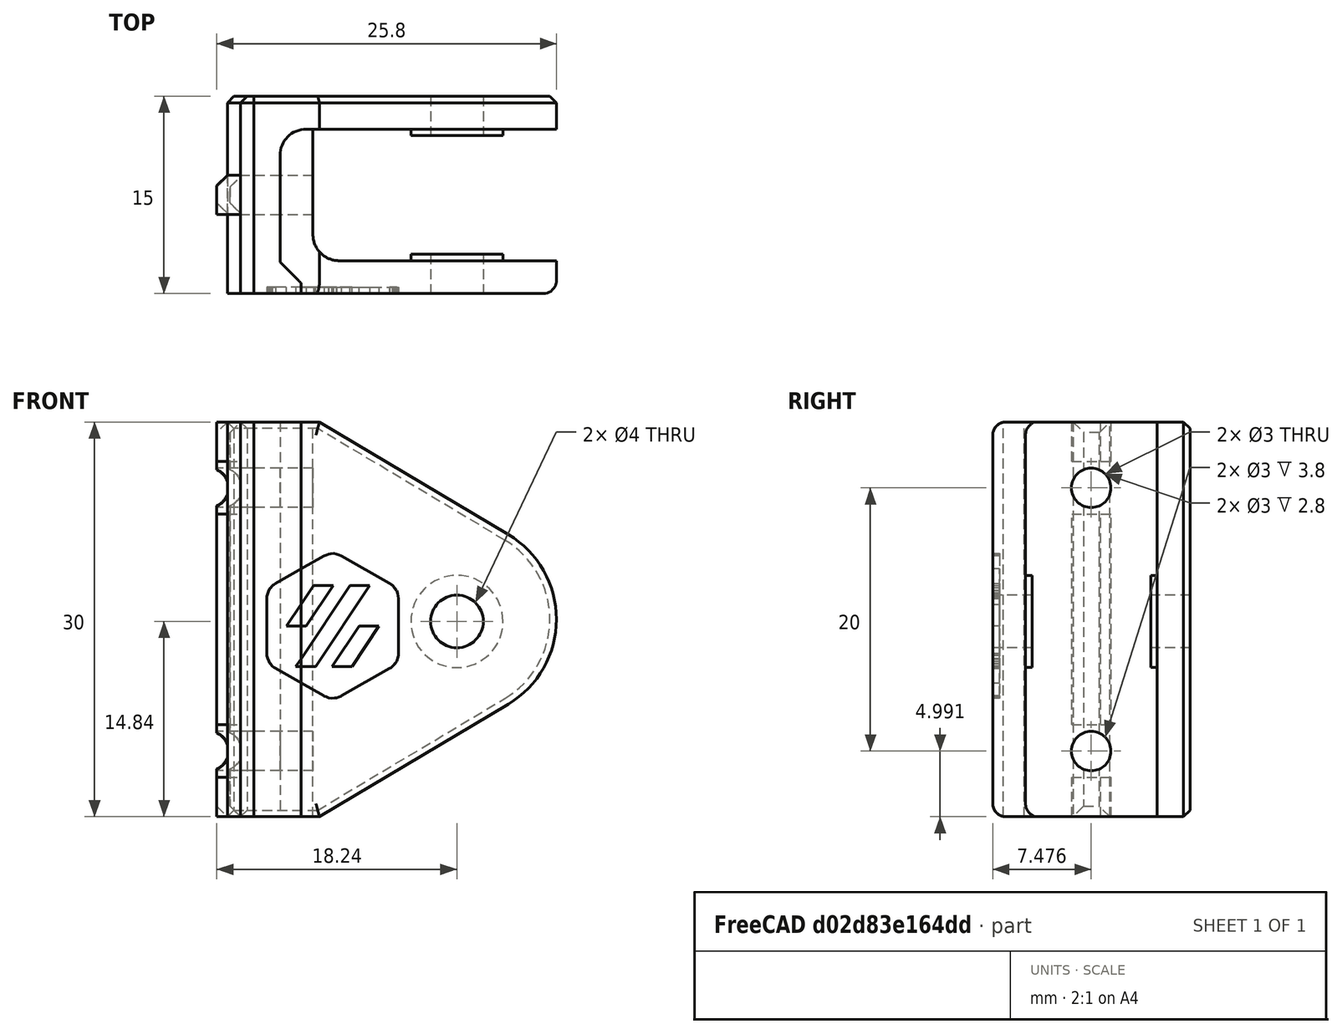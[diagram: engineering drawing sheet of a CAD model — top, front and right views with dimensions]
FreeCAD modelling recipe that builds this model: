
FCSTD DOCUMENT  (FreeCAD 0.18R16146 (Git))
Label: belt-z-idler-mount-bore-3mm
License: All rights reserved
LicenseURL: http://en.wikipedia.org/wiki/All_rights_reserved
objects: Part::Feature×5, Part::Box×4, Part::Cut×4, Part::Cylinder×2, App::Part×2, Part::MultiCommon×1, Part::MultiFuse×1, Part::Chamfer×1
note: 18 computed .brp shape members not serialized (recipe doc carries the construction recipe); baked Part::Feature solids carry a one-line shape summary decoded from their .brp

FEATURE [Part::Feature] Part__Feature014001  label="Z-Back-3mm-9wideToothedPulley001"
  Placement = pos=(1,0,0) rot=(0,0,1;0rad)
  shape: bbox 24.8 x 15 x 30 mm, 38 faces (baked)
FEATURE [Part::Feature] Part__Feature015001  label="Z-Front-3mm-9wide-ToothedPulley001"
  Placement = pos=(1,0,0) rot=(0,0,1;0rad)
  shape: bbox 21.62 x 12.5 x 30 mm, 24 faces (baked)
FEATURE [Part::Box] Box  label="Cube"
  AttacherType = Attacher::AttachEngine3D
  Height = 33
  Length = 3
  Width = 15
FEATURE [Part::Feature] Part__Feature015002  label="Z-Back-3mm-9wideToothedPulley002"
  Placement = pos=(1,0,0) rot=(0,0,1;0rad)
  shape: bbox 24.8 x 15 x 30 mm, 38 faces (baked)
FEATURE [Part::MultiCommon] Common
  Placement = pos=(-1,0,0) rot=(0,0,1;0rad)
  Shapes = -> [Box,Part__Feature015002]
FEATURE [Part::Cylinder] Cylinder
  Angle = 360
  AttacherType = Attacher::AttachEngine3D
  Height = 27
  Placement = pos=(17.44,25,14.84) rot=(1,0,0;1.5708rad)
  Radius = 2
FEATURE [Part::Cylinder] Cylinder001
  Angle = 360
  AttacherType = Attacher::AttachEngine3D
  Height = 27
  Placement = pos=(17.44,25,14.84) rot=(1,0,0;1.5708rad)
  Radius = 2
FEATURE [Part::Cut] Cut
  Base = -> Part__Feature014001
  Tool = -> Cylinder001
FEATURE [Part::Cut] Cut001
  Base = -> Part__Feature015001
  Tool = -> Cylinder
FEATURE [Part::Box] Box001  label="Cube001"
  AttacherType = Attacher::AttachEngine3D
  Height = 16
  Length = 1.8
  Placement = pos=(-0.8,6,7) rot=(0,0,1;0rad)
  Width = 3
FEATURE [Part::Box] Box002  label="Cube002"
  AttacherType = Attacher::AttachEngine3D
  Height = 3
  Length = 1.8
  Placement = pos=(-0.8,6,0) rot=(0,0,1;0rad)
  Width = 3
FEATURE [Part::Box] Box003  label="Cube003"
  AttacherType = Attacher::AttachEngine3D
  Height = 3
  Length = 1.8
  Placement = pos=(-0.8,6,27) rot=(0,0,1;0rad)
  Width = 3
FEATURE [Part::Feature] Exquisite_Curcan_Bombul_3_001001_solid  label="Exquisite_Curcan_Bombul_3_002 (Solid)"
  Placement = pos=(46,0.5,18) rot=(1,0,0;1.5708rad)
  shape: bbox 10 x 2.413 x 11 mm, 189 faces (baked)
FEATURE [Part::Feature] Exquisite_Curcan_Bombul_3_001001_solid001  label="Exquisite_Curcan_Bombul_3_002 (Solid)001"
  Placement = pos=(46,0.5,18) rot=(1,0,0;1.5708rad)
  shape: bbox 10 x 2.413 x 11 mm, 189 faces (baked)
FEATURE [Part::Cut] Cut002
  Base = -> Cut001
  Tool = -> Exquisite_Curcan_Bombul_3_001001_solid001
FEATURE [Part::Cut] Cut003
  Base = -> Cut
  Tool = -> Exquisite_Curcan_Bombul_3_001001_solid
FEATURE [App::Part] Part  label="idler-front"
  Group = -> [Cylinder,Part__Feature015001,Exquisite_Curcan_Bombul_3_001001_solid001,Cut001,Cut002]
  Origin = -> Origin
FEATURE [Part::MultiFuse] Fusion
  Shapes = -> [Box002,Box001,Box003]
FEATURE [Part::Chamfer] Chamfer
  Base = -> Fusion
  Edges = 3 edges r=0.8: [Edge3,Edge15,Edge27]
FEATURE [App::Part] Part001  label="idler-back"
  Group = -> [Exquisite_Curcan_Bombul_3_001001_solid,Part__Feature014001,Cylinder001,Cut,Cut003,Part__Feature015002,Box,Common,Box003,Box001,Box002,Fusion,Chamfer]
  Origin = -> Origin001
